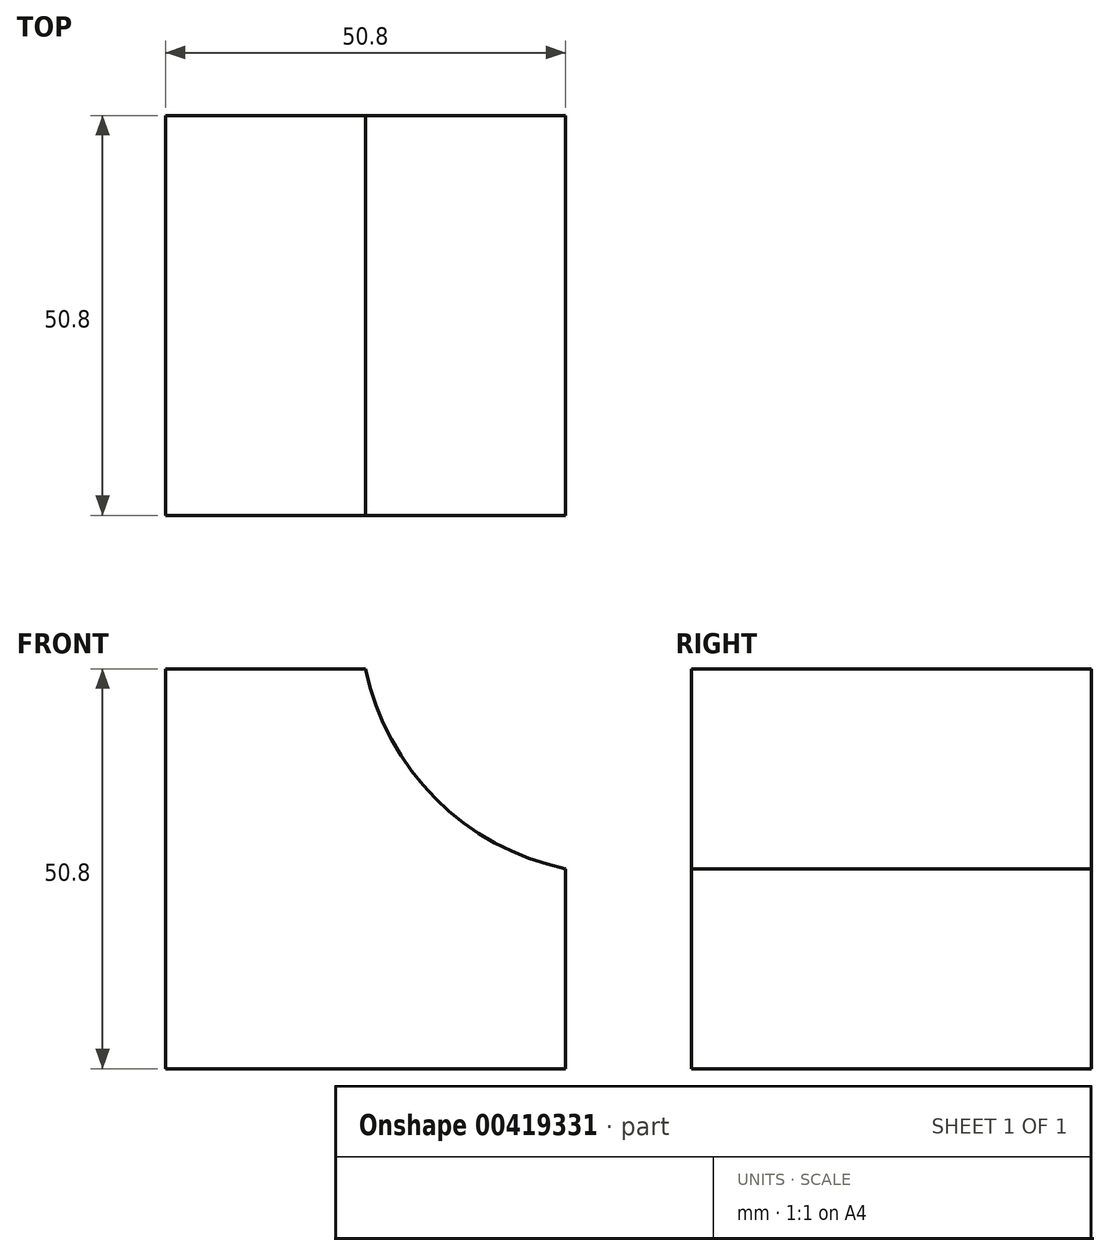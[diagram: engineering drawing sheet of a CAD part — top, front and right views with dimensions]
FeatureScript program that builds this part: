
annotation { "Feature Type Name" : "Feature", "Feature Type Description" : "" }
export const myFeature = defineFeature(function(context is Context, id is Id, definition is map)
    precondition{}
    {
        {
            var Q0;
            Q0=qCreatedBy(makeId("Front.planeOp"),FACE);
            var sketch = newSketch(context, id + "F0", { "sketchPlane" : qUnion([Q0])});
            skLineSegment(sketch, "E0", {"start": v(0, 0) * mm, "end": v(-50.8, 0) * mm});
            skLineSegment(sketch, "E1", {"start": v(-50.8, 0) * mm, "end": v(-50.8, 50.8) * mm});
            skLineSegment(sketch, "E2", {"start": v(-50.8, 50.8) * mm, "end": v(-25.4, 50.8) * mm});
            skLineSegment(sketch, "E3", {"start": v(0, 25.4) * mm, "end": v(0, 0) * mm});
            skArc(sketch, "E4", {"start": v(-25.4, 50.8) * mm, "mid": v(-16.5, 34.3) * mm, "end": v(0, 25.4) * mm});
            skSolve(sketch);
        }
        {
            var Q0;
            Q0 = qSketchRegion(id + "F0", true);
            extrude(context, id + "F1", {"entities" : qUnion([Q0]), "depth" : 50.8 * mm});
        }
    });
